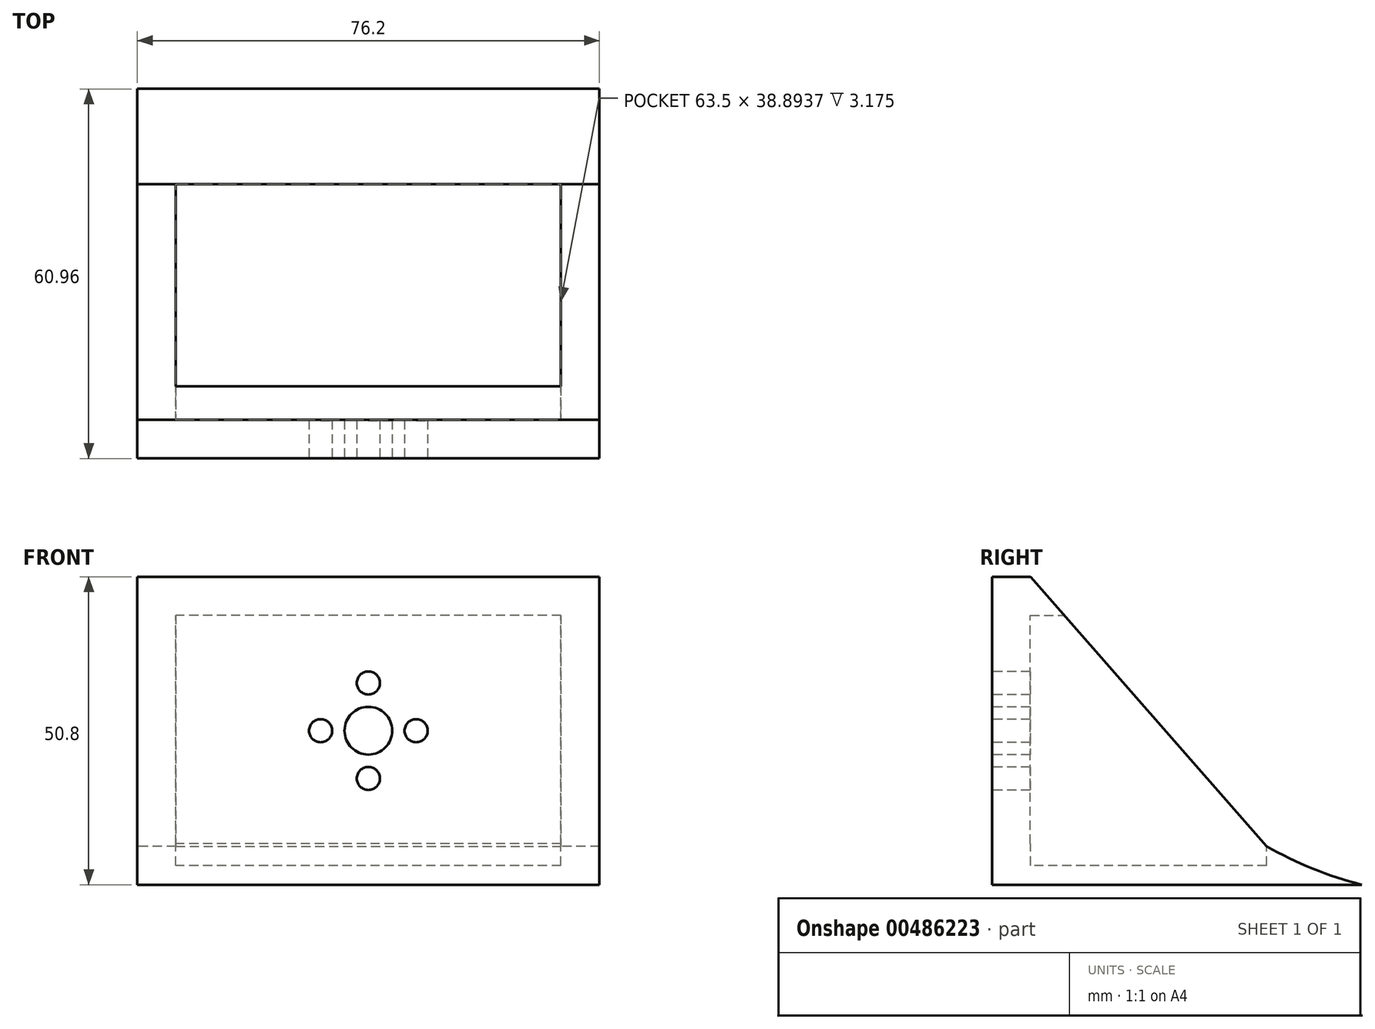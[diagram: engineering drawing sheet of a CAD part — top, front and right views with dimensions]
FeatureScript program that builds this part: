
annotation { "Feature Type Name" : "Feature", "Feature Type Description" : "" }
export const myFeature = defineFeature(function(context is Context, id is Id, definition is map)
    precondition{}
    {
        {
            var Q0;
            Q0=qCreatedBy(makeId("Right.planeOp"),FACE);
            var sketch = newSketch(context, id + "F0", { "sketchPlane" : qUnion([Q0])});
            skLineSegment(sketch, "E0", {"start": v(0, 0) * mm, "end": v(16.71, 0) * mm});
            skLineSegment(sketch, "E1", {"start": v(16.71, 0) * mm, "end": v(-34.09, 0) * mm});
            skLineSegment(sketch, "E2", {"start": v(-34.09, 0) * mm, "end": v(-34.09, 50.8) * mm});
            skLineSegment(sketch, "E3", {"start": v(-34.09, 50.8) * mm, "end": v(-27.74, 50.8) * mm});
            skLineSegment(sketch, "E4", {"start": v(-27.74, 50.8) * mm, "end": v(16.71, 0) * mm});
            skSolve(sketch);
        }
        {
            var Q0;
            Q0 = qSketchRegion(id + "F0", true);
            extrude(context, id + "F1", {"entities" : qUnion([Q0]), "depth" : 76.2 * mm, "offsetDistance" : 25.4 * mm});
        }
        {
            var Q0;
            Q0=makeQuery(id+"F1.opExtrude","SWEPT_FACE",FACE,{"disambiguationData":[OSD([sQuery(id+"F0.wireOp",EDGE,"E4")])]});
            shell(context, id + "F2", {"entities" : qUnion([Q0]), "thickness" : 6.35 * mm});
        }
        {
            var Q0;
            Q0=makeQuery(id+"F1.opExtrude","SWEPT_FACE",FACE,{"disambiguationData":[OSD([sQuery(id+"F0.wireOp",EDGE,"E1")])]});
            var sketch = newSketch(context, id + "F3", { "sketchPlane" : qUnion([Q0])});
            skLineSegment(sketch, "E5", {"start": v(0, 34.09) * mm, "end": v(0, -26.87) * mm});
            skLineSegment(sketch, "E6", {"start": v(0, -26.87) * mm, "end": v(76.2, -26.87) * mm});
            skLineSegment(sketch, "E7", {"start": v(76.2, -26.87) * mm, "end": v(76.2, 34.09) * mm});
            skLineSegment(sketch, "E8", {"start": v(76.2, 34.09) * mm, "end": v(0, 34.09) * mm});
            skSolve(sketch);
        }
        {
            var Q0;
            {var subQ2=sQuery(id+"F3.wireOp",EDGE,"E8");Q0=makeQuery(id+"F3.imprint","IMPRINT",FACE,{"disambiguationData":[TD([[makeQuery(id+"F3.imprint","IMPRINT",EDGE,{"derivedFrom":subQ2}),1.0]])]});}
            var Q1;
            {var subQ2=sQuery(id+"F3.wireOp",EDGE,"E6");Q1=makeQuery(id+"F3.imprint","IMPRINT",FACE,{"disambiguationData":[TD([[makeQuery(id+"F3.imprint","IMPRINT",EDGE,{"derivedFrom":subQ2}),1.0]])]});}
            extrude(context, id + "F4", {"entities" : qUnion([Q0, Q1]), "operationType" : NewBodyOperationType.ADD, "oppositeDirection" : true, "depth" : 6.35 * mm, "offsetDistance" : 25.4 * mm});
        }
        {
            var Q0;
            Q0=makeQuery(id+"F4.boolean.opBoolean","MERGE",FACE,{"derivedFrom":[makeQuery(id+"F1.opExtrude","CAP_FACE",FACE,{"disambiguationData":[OSD([sQuery(id+"F0.wireOp",EDGE,"E1"),sQuery(id+"F0.wireOp",EDGE,"E2"),sQuery(id+"F0.wireOp",EDGE,"E3"),sQuery(id+"F0.wireOp",EDGE,"E4")])],"isStart":false}),makeQuery(id+"F4.opExtrude","SWEPT_FACE",FACE,{"disambiguationData":[OSD([sQuery(id+"F3.wireOp",EDGE,"E7")])]})]});
            var sketch = newSketch(context, id + "F5", { "sketchPlane" : qUnion([Q0])});
            skArc(sketch, "E9", {"start": v(11.16, 6.35) * mm, "mid": v(18.8, 2.64) * mm, "end": v(26.87, 0) * mm});
            skLineSegment(sketch, "E10", {"start": v(26.87, 0) * mm, "end": v(26.87, 6.35) * mm});
            skLineSegment(sketch, "E11", {"start": v(26.87, 6.35) * mm, "end": v(11.16, 6.35) * mm});
            skSolve(sketch);
        }
        {
            var Q0;
            Q0 = qSketchRegion(id + "F5", true);
            extrude(context, id + "F6", {"entities" : qUnion([Q0]), "operationType" : NewBodyOperationType.REMOVE, "oppositeDirection" : true, "depth" : 76.2 * mm, "offsetDistance" : 25.4 * mm});
        }
        {
            var Q0;
            Q0=makeQuery(id+"F1.opExtrude","SWEPT_FACE",FACE,{"disambiguationData":[OSD([sQuery(id+"F0.wireOp",EDGE,"E2")])]});
            var sketch = newSketch(context, id + "F7", { "sketchPlane" : qUnion([Q0])});
            skLineSegment(sketch, "E12", {"start": v(38.1, 50.8) * mm, "end": v(38.1, 0) * mm, "construction": true});
            skLineSegment(sketch, "E13", {"start": v(38.1, 0) * mm, "end": v(38.1, 25.4) * mm, "construction": true});
            skLineSegment(sketch, "E14", {"start": v(38.1, 25.4) * mm, "end": v(0, 25.4) * mm, "construction": true});
            skLineSegment(sketch, "E15", {"start": v(0, 25.4) * mm, "end": v(76.2, 25.4) * mm, "construction": true});
            skCircle(sketch, "E16", {"center": v(38.1, 25.4) * mm, "radius": 3.94 * mm});
            skLineSegment(sketch, "E17", {"start": v(38.1, 25.4) * mm, "end": v(38.1, 21.46) * mm, "construction": true});
            skLineSegment(sketch, "E18", {"start": v(38.1, 21.46) * mm, "end": v(38.1, 35.18) * mm, "construction": true});
            skLineSegment(sketch, "E19", {"start": v(38.1, 35.18) * mm, "end": v(38.1, 29.34) * mm, "construction": true});
            skLineSegment(sketch, "E20", {"start": v(38.1, 29.34) * mm, "end": v(38.1, 15.62) * mm, "construction": true});
            skLineSegment(sketch, "E21", {"start": v(38.1, 15.62) * mm, "end": v(38.1, 25.4) * mm, "construction": true});
            skLineSegment(sketch, "E22", {"start": v(38.1, 29.34) * mm, "end": v(38.1, 31.37) * mm, "construction": true});
            skLineSegment(sketch, "E23", {"start": v(38.1, 31.37) * mm, "end": v(38.1, 35.18) * mm, "construction": true});
            skCircle(sketch, "E24", {"center": v(38.1, 33.27) * mm, "radius": 1.9 * mm});
            skCircle(sketch, "E25.MirrorC", {"center": v(38.1, 17.53) * mm, "radius": 1.9 * mm});
            skLineSegment(sketch, "E26", {"start": v(42.04, 25.4) * mm, "end": v(28.32, 25.4) * mm, "construction": true});
            skLineSegment(sketch, "E27", {"start": v(34.16, 25.4) * mm, "end": v(32.13, 25.4) * mm, "construction": true});
            skLineSegment(sketch, "E28", {"start": v(32.13, 25.4) * mm, "end": v(28.32, 25.4) * mm, "construction": true});
            skCircle(sketch, "E29", {"center": v(30.23, 25.4) * mm, "radius": 1.9 * mm});
            skCircle(sketch, "E30.MirrorC", {"center": v(45.97, 25.4) * mm, "radius": 1.9 * mm});
            skSolve(sketch);
        }
        {
            var Q0;
            Q0 = qSketchRegion(id + "F7", true);
            extrude(context, id + "F8", {"entities" : qUnion([Q0]), "operationType" : NewBodyOperationType.REMOVE, "oppositeDirection" : true, "depth" : 25.4 * mm, "offsetDistance" : 25.4 * mm});
        }
        {
            var Q0;
            Q0=makeQuery(id+"F4.boolean.opBoolean","MERGE",FACE,{"derivedFrom":[makeQuery(id+"F2.opShell","OFFSET_FACE",FACE,{"disambiguationData":[OSD([sQuery(id+"F0.wireOp",EDGE,"E1")])]}),makeQuery(id+"F4.opExtrude","CAP_FACE",FACE,{"disambiguationData":[OSD([sQuery(id+"F3.wireOp",EDGE,"E5"),sQuery(id+"F3.wireOp",EDGE,"E6"),sQuery(id+"F3.wireOp",EDGE,"E7"),sQuery(id+"F3.wireOp",EDGE,"E8")])],"isStart":false})]});
            var sketch = newSketch(context, id + "F9", { "sketchPlane" : qUnion([Q0])});
            skLineSegment(sketch, "E31.bottom", {"start": v(69.85, -27.74) * mm, "end": v(6.35, -27.74) * mm});
            skLineSegment(sketch, "E31.top", {"start": v(69.85, 11.16) * mm, "end": v(6.35, 11.16) * mm});
            skLineSegment(sketch, "E31.left", {"start": v(69.85, -27.74) * mm, "end": v(69.85, 11.16) * mm});
            skLineSegment(sketch, "E31.right", {"start": v(6.35, -27.74) * mm, "end": v(6.35, 11.16) * mm});
            skSolve(sketch);
        }
        {
            var Q0;
            Q0 = qSketchRegion(id + "F9", true);
            extrude(context, id + "F10", {"entities" : qUnion([Q0]), "operationType" : NewBodyOperationType.REMOVE, "oppositeDirection" : true, "depth" : 3.17 * mm, "offsetDistance" : 25.4 * mm});
        }
        {
            var Q0;
            Q0=makeQuery(id+"F10.boolean.opBoolean","MERGE",FACE,{"derivedFrom":[makeQuery(id+"F2.opShell","OFFSET_FACE",FACE,{"disambiguationData":[OSD([sQuery(id+"F0.wireOp",EDGE,"E2")])]})],"fromTools":[makeQuery(id+"F10.opExtrude","SWEPT_FACE",FACE,{"disambiguationData":[OSD([sQuery(id+"F9.wireOp",EDGE,"E31.bottom")])]})]});
            var sketch = newSketch(context, id + "F11", { "sketchPlane" : qUnion([Q0])});
            skLineSegment(sketch, "E32.bottom", {"start": v(-69.85, 44.45) * mm, "end": v(-6.35, 44.45) * mm});
            skLineSegment(sketch, "E32.top", {"start": v(-69.85, 6.78) * mm, "end": v(-6.35, 6.78) * mm});
            skLineSegment(sketch, "E32.left", {"start": v(-69.85, 44.45) * mm, "end": v(-69.85, 6.78) * mm});
            skLineSegment(sketch, "E32.right", {"start": v(-6.35, 44.45) * mm, "end": v(-6.35, 6.78) * mm});
            skSolve(sketch);
        }
        {
            var Q0;
            Q0 = qSketchRegion(id + "F11", true);
            extrude(context, id + "F12", {"entities" : qUnion([Q0]), "operationType" : NewBodyOperationType.REMOVE, "oppositeDirection" : true, "depth" : 0.08 * mm, "offsetDistance" : 25.4 * mm});
        }
    });
